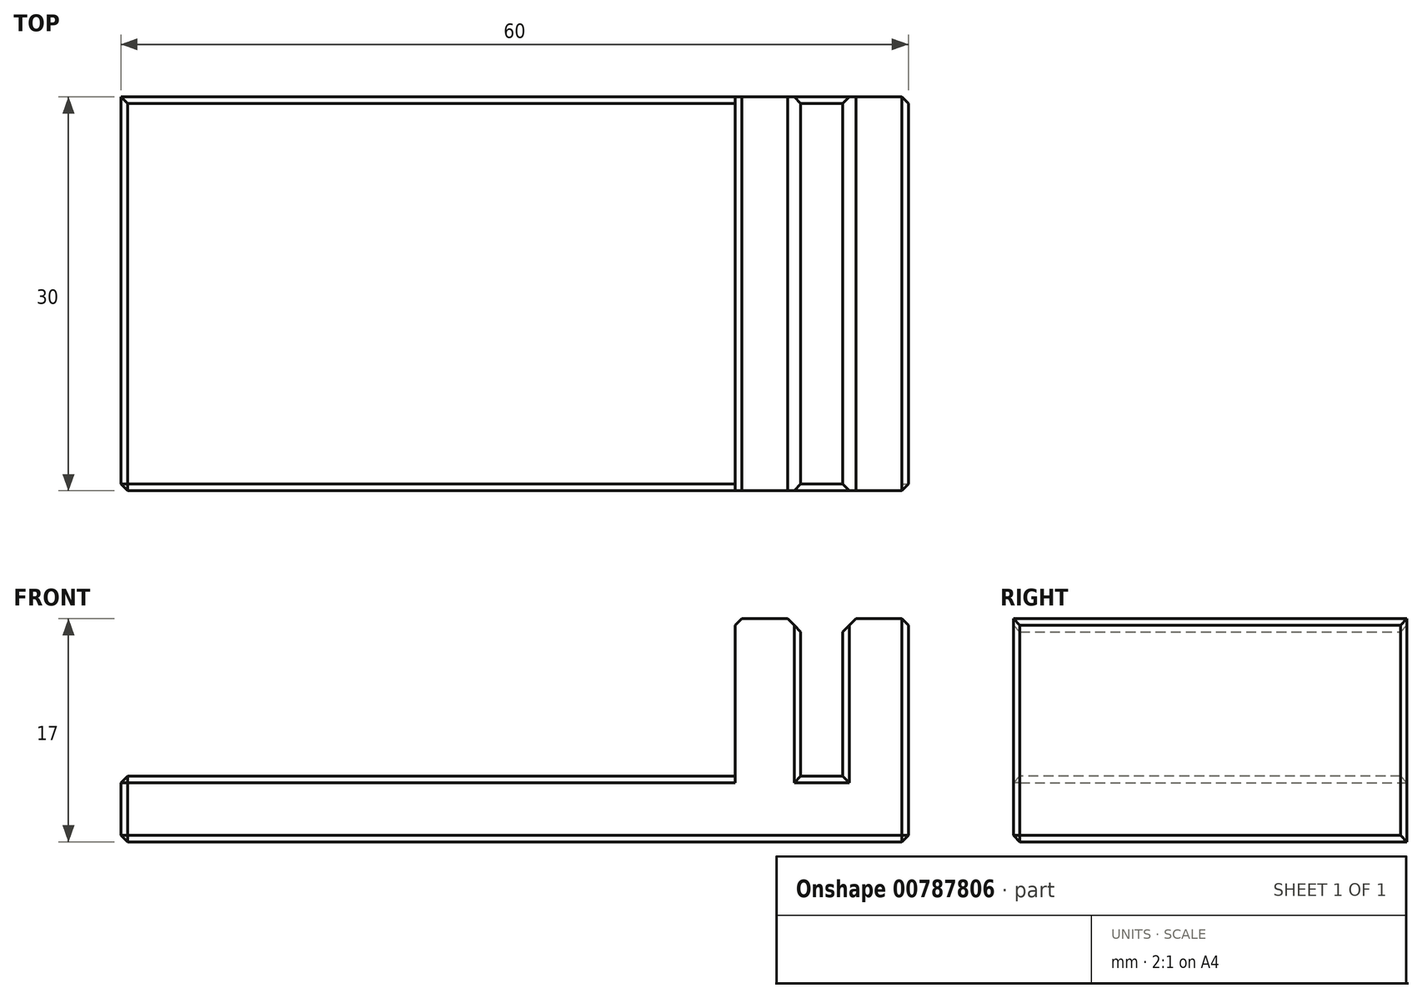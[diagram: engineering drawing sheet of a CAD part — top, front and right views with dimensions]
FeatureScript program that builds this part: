
annotation { "Feature Type Name" : "Feature", "Feature Type Description" : "" }
export const myFeature = defineFeature(function(context is Context, id is Id, definition is map)
    precondition{}
    {
        {
            var Q0;
            Q0=qCreatedBy(makeId("Top.planeOp"),FACE);
            var sketch = newSketch(context, id + "F0", { "sketchPlane" : qUnion([Q0])});
            skLineSegment(sketch, "E0.bottom", {"start": v(30, 15) * mm, "end": v(-30, 15) * mm});
            skLineSegment(sketch, "E0.top", {"start": v(30, -15) * mm, "end": v(-30, -15) * mm});
            skLineSegment(sketch, "E0.left", {"start": v(30, 15) * mm, "end": v(30, -15) * mm});
            skLineSegment(sketch, "E0.right", {"start": v(-30, 15) * mm, "end": v(-30, -15) * mm});
            skPoint(sketch, "E0.middle", {"position": v(0, 0) * mm});
            skSolve(sketch);
        }
        {
            var Q0;
            Q0=makeQuery(id+"F0.imprint","IMPRINT",FACE,{"disambiguationData":[TD([[makeQuery(id+"F0.imprint","IMPRINT",EDGE,{"derivedFrom":sQuery(id+"F0.wireOp",EDGE,"E0.bottom")}),1.0]])]});
            extrude(context, id + "F1", {"entities" : qUnion([Q0]), "depth" : 5 * mm, "offsetDistance" : 25 * mm});
        }
        {
            var Q0;
            Q0=makeQuery(id+"F1.opExtrude","CAP_FACE",FACE,{"disambiguationData":[OSD([sQuery(id+"F0.wireOp",EDGE,"E0.bottom"),sQuery(id+"F0.wireOp",EDGE,"E0.top"),sQuery(id+"F0.wireOp",EDGE,"E0.left"),sQuery(id+"F0.wireOp",EDGE,"E0.right")])],"isStart":false});
            var sketch = newSketch(context, id + "F2", { "sketchPlane" : qUnion([Q0])});
            skLineSegment(sketch, "E1.bottom", {"start": v(30, 15) * mm, "end": v(25, 15) * mm});
            skLineSegment(sketch, "E1.top", {"start": v(30, -15) * mm, "end": v(25, -15) * mm});
            skLineSegment(sketch, "E1.left", {"start": v(30, 15) * mm, "end": v(30, -15) * mm});
            skLineSegment(sketch, "E1.right", {"start": v(25, 15) * mm, "end": v(25, -15) * mm});
            skLineSegment(sketch, "E2.bottom", {"start": v(21.8, 15) * mm, "end": v(16.8, 15) * mm});
            skLineSegment(sketch, "E2.top", {"start": v(21.8, -15) * mm, "end": v(16.8, -15) * mm});
            skLineSegment(sketch, "E2.left", {"start": v(21.8, 15) * mm, "end": v(21.8, -15) * mm});
            skLineSegment(sketch, "E2.right", {"start": v(16.8, 15) * mm, "end": v(16.8, -15) * mm});
            skSolve(sketch);
        }
        {
            var Q0;
            Q0=makeQuery(id+"F2.imprint","IMPRINT",FACE,{"disambiguationData":[TD([[makeQuery(id+"F2.imprint","IMPRINT",EDGE,{"derivedFrom":sQuery(id+"F2.wireOp",EDGE,"E2.bottom")}),1.0]])]});
            var Q1;
            Q1=makeQuery(id+"F2.imprint","IMPRINT",FACE,{"disambiguationData":[TD([[makeQuery(id+"F2.imprint","IMPRINT",EDGE,{"derivedFrom":sQuery(id+"F2.wireOp",EDGE,"E1.bottom")}),1.0]])]});
            extrude(context, id + "F3", {"entities" : qUnion([Q0, Q1]), "operationType" : NewBodyOperationType.ADD, "depth" : 12 * mm, "offsetDistance" : 25 * mm});
        }
        {
            var Q0;
            Q0=makeQuery(id+"F3.opExtrude","CAP_EDGE",EDGE,{"disambiguationData":[OSD([sQuery(id+"F2.wireOp",EDGE,"E2.left")])],"isStart":false});
            var Q1;
            Q1=makeQuery(id+"F3.opExtrude","CAP_EDGE",EDGE,{"disambiguationData":[OSD([sQuery(id+"F2.wireOp",EDGE,"E1.right")])],"isStart":false});
            chamfer(context, id + "F4", {"entities" : qUnion([Q0, Q1]), "width" : 1 * mm, "tangentPropagation" : true});
        }
        {
            var Q0;
            {var subQ0=sQuery(id+"F0.wireOp",EDGE,"E0.right");var subQ1=sQuery(id+"F0.wireOp",EDGE,"E0.top");Q0=makeQuery(id+"F3.boolean.opBoolean","SPLIT",EDGE,{"disambiguationData":[TD([makeQuery(id+"F1.opExtrude","SWEPT_FACE",FACE,{"disambiguationData":[OSD([subQ0])]})])],"derivedFrom":makeQuery(id+"F1.opExtrude","CAP_EDGE",EDGE,{"disambiguationData":[OSD([subQ1])],"isStart":false})});}
            var Q1;
            Q1=makeQuery(id+"F1.opExtrude","CAP_EDGE",EDGE,{"disambiguationData":[OSD([sQuery(id+"F0.wireOp",EDGE,"E0.right")])],"isStart":false});
            var Q2;
            {var subQ0=sQuery(id+"F0.wireOp",EDGE,"E0.right");var subQ1=sQuery(id+"F0.wireOp",EDGE,"E0.bottom");Q2=makeQuery(id+"F3.boolean.opBoolean","SPLIT",EDGE,{"disambiguationData":[TD([makeQuery(id+"F1.opExtrude","SWEPT_FACE",FACE,{"disambiguationData":[OSD([subQ0])]})])],"derivedFrom":makeQuery(id+"F1.opExtrude","CAP_EDGE",EDGE,{"disambiguationData":[OSD([subQ1])],"isStart":false})});}
            var Q3;
            Q3=makeQuery(id+"F1.opExtrude","SWEPT_EDGE",EDGE,{"disambiguationData":[OSD([sQuery(id+"F0.wireOp",EDGE,"E0.top"),sQuery(id+"F0.wireOp",EDGE,"E0.right")])]});
            var Q4;
            Q4=makeQuery(id+"F1.opExtrude","CAP_EDGE",EDGE,{"disambiguationData":[OSD([sQuery(id+"F0.wireOp",EDGE,"E0.top")])],"isStart":true});
            var Q5;
            {var subQ0=sQuery(id+"F0.wireOp",EDGE,"E0.top");Q5=makeQuery(id+"F3.boolean.opBoolean","SPLIT",EDGE,{"disambiguationData":[TD([makeQuery(id+"F3.opExtrude","SWEPT_FACE",FACE,{"disambiguationData":[OSD([sQuery(id+"F2.wireOp",EDGE,"E1.right")])]})])],"derivedFrom":makeQuery(id+"F1.opExtrude","CAP_EDGE",EDGE,{"disambiguationData":[OSD([subQ0])],"isStart":false})});}
            var Q6;
            Q6=makeQuery(id+"F1.opExtrude","CAP_EDGE",EDGE,{"disambiguationData":[OSD([sQuery(id+"F0.wireOp",EDGE,"E0.left")])],"isStart":true});
            var Q7;
            Q7=makeQuery(id+"F3.opExtrude","CAP_EDGE",EDGE,{"disambiguationData":[OSD([sQuery(id+"F2.wireOp",EDGE,"E2.right")])],"isStart":false});
            var Q8;
            Q8=makeQuery(id+"F3.opExtrude","CAP_EDGE",EDGE,{"disambiguationData":[OSD([sQuery(id+"F2.wireOp",EDGE,"E1.left")])],"isStart":false});
            var Q9;
            Q9=makeQuery(id+"F1.opExtrude","CAP_EDGE",EDGE,{"disambiguationData":[OSD([sQuery(id+"F0.wireOp",EDGE,"E0.right")])],"isStart":true});
            var Q10;
            Q10=makeQuery(id+"F3.boolean.opBoolean","MERGE",EDGE,{"derivedFrom":[makeQuery(id+"F1.opExtrude","SWEPT_EDGE",EDGE,{"disambiguationData":[OSD([sQuery(id+"F0.wireOp",EDGE,"E0.top"),sQuery(id+"F0.wireOp",EDGE,"E0.left")])]}),makeQuery(id+"F3.opExtrude","SWEPT_EDGE",EDGE,{"disambiguationData":[OSD([sQuery(id+"F2.wireOp",EDGE,"E1.top"),sQuery(id+"F2.wireOp",EDGE,"E1.left")])]})]});
            var Q11;
            Q11=makeQuery(id+"F3.boolean.opBoolean","MERGE",EDGE,{"derivedFrom":[makeQuery(id+"F1.opExtrude","SWEPT_EDGE",EDGE,{"disambiguationData":[OSD([sQuery(id+"F0.wireOp",EDGE,"E0.bottom"),sQuery(id+"F0.wireOp",EDGE,"E0.left")])]}),makeQuery(id+"F3.opExtrude","SWEPT_EDGE",EDGE,{"disambiguationData":[OSD([sQuery(id+"F2.wireOp",EDGE,"E1.bottom"),sQuery(id+"F2.wireOp",EDGE,"E1.left")])]})]});
            var Q12;
            {var subQ0=sQuery(id+"F0.wireOp",EDGE,"E0.bottom");Q12=makeQuery(id+"F3.boolean.opBoolean","SPLIT",EDGE,{"disambiguationData":[TD([makeQuery(id+"F3.opExtrude","SWEPT_FACE",FACE,{"disambiguationData":[OSD([sQuery(id+"F2.wireOp",EDGE,"E1.right")])]})])],"derivedFrom":makeQuery(id+"F1.opExtrude","CAP_EDGE",EDGE,{"disambiguationData":[OSD([subQ0])],"isStart":false})});}
            var Q13;
            Q13=makeQuery(id+"F3.opExtrude","SWEPT_EDGE",EDGE,{"disambiguationData":[OSD([sQuery(id+"F0.wireOp",EDGE,"E0.bottom"),sQuery(id+"F2.wireOp",EDGE,"E2.bottom"),sQuery(id+"F2.wireOp",EDGE,"E2.left")])]});
            var Q14;
            Q14=makeQuery(id+"F3.opExtrude","SWEPT_EDGE",EDGE,{"disambiguationData":[OSD([sQuery(id+"F0.wireOp",EDGE,"E0.bottom"),sQuery(id+"F2.wireOp",EDGE,"E1.bottom"),sQuery(id+"F2.wireOp",EDGE,"E1.right")])]});
            var Q15;
            Q15=makeQuery(id+"F3.opExtrude","SWEPT_EDGE",EDGE,{"disambiguationData":[OSD([sQuery(id+"F0.wireOp",EDGE,"E0.top"),sQuery(id+"F2.wireOp",EDGE,"E1.top"),sQuery(id+"F2.wireOp",EDGE,"E1.right")])]});
            var Q16;
            Q16=makeQuery(id+"F3.opExtrude","SWEPT_EDGE",EDGE,{"disambiguationData":[OSD([sQuery(id+"F0.wireOp",EDGE,"E0.top"),sQuery(id+"F2.wireOp",EDGE,"E2.top"),sQuery(id+"F2.wireOp",EDGE,"E2.left")])]});
            chamfer(context, id + "F5", {"entities" : qUnion([Q0, Q1, Q2, Q3, Q4, Q5, Q6, Q7, Q8, Q9, Q10, Q11, Q12, Q13, Q14, Q15, Q16]), "width" : 0.5 * mm, "tangentPropagation" : true});
        }
    });
